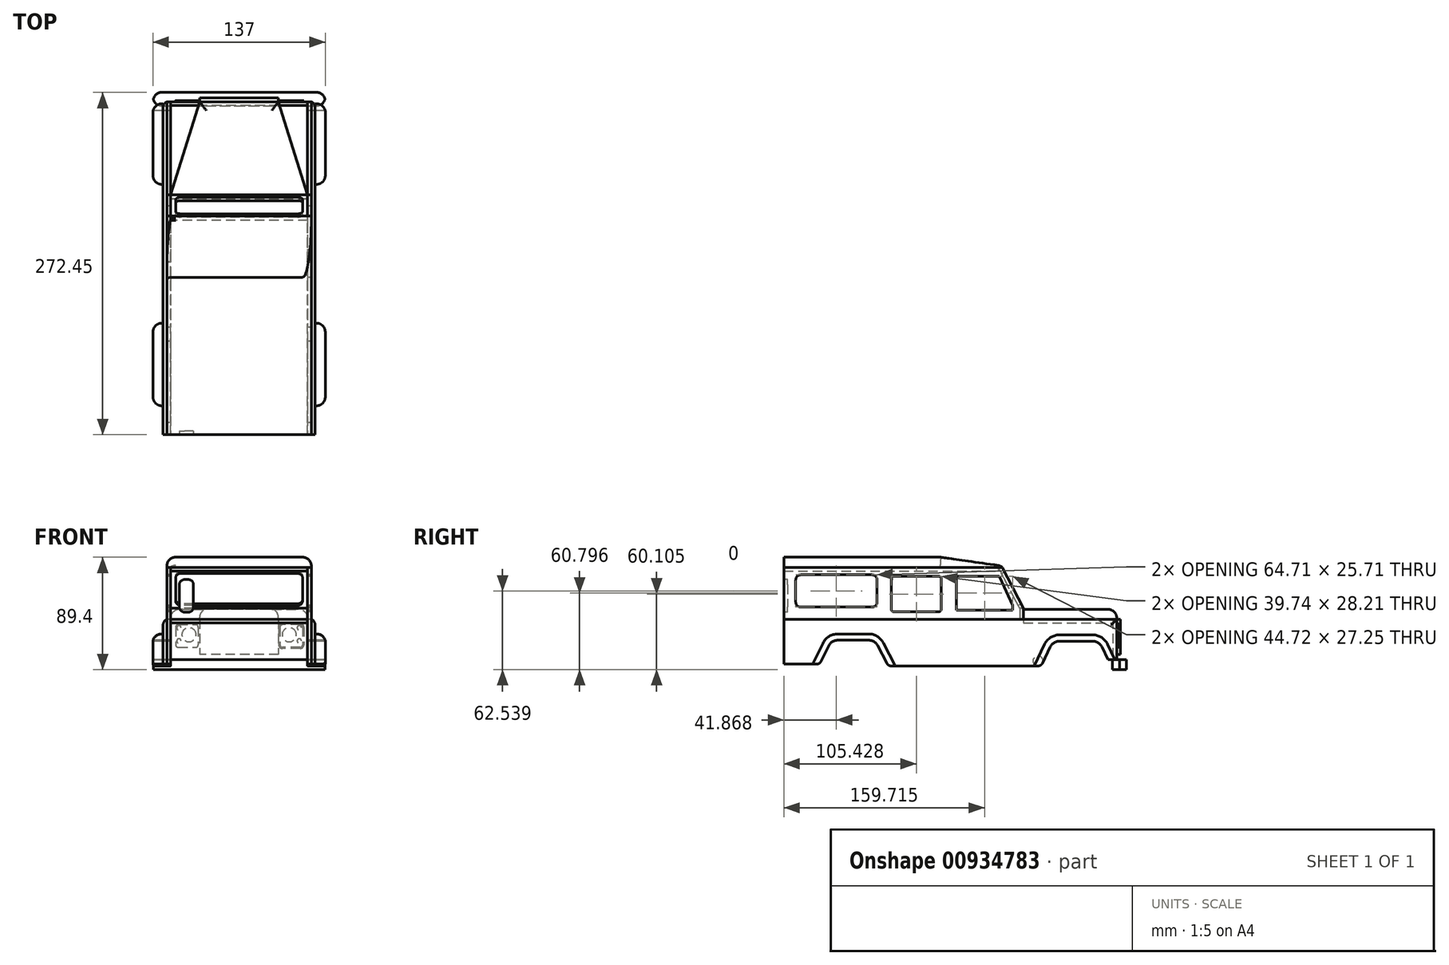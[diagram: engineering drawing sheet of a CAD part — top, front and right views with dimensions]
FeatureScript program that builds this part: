
annotation { "Feature Type Name" : "Feature", "Feature Type Description" : "" }
export const myFeature = defineFeature(function(context is Context, id is Id, definition is map)
    precondition{}
    {
        {
            var Q0;
            Q0=qCreatedBy(makeId("Right.planeOp"),FACE);
            var sketch = newSketch(context, id + "F0", { "sketchPlane" : qUnion([Q0])});
            skLineSegment(sketch, "E0", {"start": v(6.05, 16.68) * mm, "end": v(6.05, 93.72) * mm});
            skLineSegment(sketch, "E1", {"start": v(6.05, 93.72) * mm, "end": v(180.01, 93.72) * mm});
            skLineSegment(sketch, "E2", {"start": v(180.01, 93.72) * mm, "end": v(196.81, 61.17) * mm});
            skLineSegment(sketch, "E3", {"start": v(196.81, 61.17) * mm, "end": v(196.81, 52.3) * mm});
            skLineSegment(sketch, "E4", {"start": v(196.81, 52.3) * mm, "end": v(270.97, 52.3) * mm});
            skLineSegment(sketch, "E5", {"start": v(270.97, 52.3) * mm, "end": v(270.97, 20.32) * mm});
            skLineSegment(sketch, "E6", {"start": v(270.97, 20.32) * mm, "end": v(263.87, 20.32) * mm});
            skLineSegment(sketch, "E7", {"start": v(263.87, 20.32) * mm, "end": v(259.15, 30.3) * mm});
            skLineSegment(sketch, "E8", {"start": v(251.92, 34.88) * mm, "end": v(225.3, 34.88) * mm});
            skLineSegment(sketch, "E9", {"start": v(218.07, 30.32) * mm, "end": v(211.96, 17.47) * mm});
            skLineSegment(sketch, "E10", {"start": v(208.35, 15.2) * mm, "end": v(91.6, 15.2) * mm});
            skLineSegment(sketch, "E11", {"start": v(88.04, 17.34) * mm, "end": v(80.75, 31.36) * mm});
            skLineSegment(sketch, "E12", {"start": v(73.66, 35.66) * mm, "end": v(48.95, 35.66) * mm});
            skLineSegment(sketch, "E13", {"start": v(41.76, 31.17) * mm, "end": v(35.78, 18.92) * mm});
            skLineSegment(sketch, "E14", {"start": v(32.18, 16.68) * mm, "end": v(6.05, 16.68) * mm});
            skPoint(sketch, "E15.visualSharp", {"position": v(78.51, 35.66) * mm});
            skArc(sketch, "E15.filletArc", {"start": v(80.75, 31.36) * mm, "mid": v(77.8, 34.5) * mm, "end": v(73.66, 35.66) * mm});
            skPoint(sketch, "E16.visualSharp", {"position": v(43.95, 35.66) * mm});
            skArc(sketch, "E16.filletArc", {"start": v(48.95, 35.66) * mm, "mid": v(44.7, 34.45) * mm, "end": v(41.76, 31.17) * mm});
            skPoint(sketch, "E17.visualSharp", {"position": v(220.24, 34.88) * mm});
            skArc(sketch, "E17.filletArc", {"start": v(225.3, 34.88) * mm, "mid": v(221.02, 33.65) * mm, "end": v(218.07, 30.32) * mm});
            skPoint(sketch, "E18.visualSharp", {"position": v(256.99, 34.88) * mm});
            skArc(sketch, "E18.filletArc", {"start": v(259.15, 30.3) * mm, "mid": v(256.2, 33.64) * mm, "end": v(251.92, 34.88) * mm});
            skLineSegment(sketch, "E19", {"start": v(19.56, 87.71) * mm, "end": v(76.27, 87.71) * mm});
            skLineSegment(sketch, "E20", {"start": v(80.27, 83.71) * mm, "end": v(80.27, 66) * mm});
            skLineSegment(sketch, "E21", {"start": v(76.27, 62) * mm, "end": v(19.56, 62) * mm});
            skLineSegment(sketch, "E22", {"start": v(15.56, 66) * mm, "end": v(15.56, 83.71) * mm});
            skPoint(sketch, "E23.visualSharp", {"position": v(15.56, 87.71) * mm});
            skArc(sketch, "E23.filletArc", {"start": v(19.56, 87.71) * mm, "mid": v(16.73, 86.54) * mm, "end": v(15.56, 83.71) * mm});
            skPoint(sketch, "E24.visualSharp", {"position": v(80.27, 87.71) * mm});
            skArc(sketch, "E24.filletArc", {"start": v(80.27, 83.71) * mm, "mid": v(79.1, 86.54) * mm, "end": v(76.27, 87.71) * mm});
            skPoint(sketch, "E25.visualSharp", {"position": v(80.27, 62) * mm});
            skArc(sketch, "E25.filletArc", {"start": v(76.27, 62) * mm, "mid": v(79.1, 63.18) * mm, "end": v(80.27, 66) * mm});
            skPoint(sketch, "E26.visualSharp", {"position": v(15.56, 62) * mm});
            skArc(sketch, "E26.filletArc", {"start": v(15.56, 66) * mm, "mid": v(16.73, 63.18) * mm, "end": v(19.56, 62) * mm});
            skLineSegment(sketch, "E27", {"start": v(93.6, 86.53) * mm, "end": v(129.35, 86.53) * mm});
            skLineSegment(sketch, "E28", {"start": v(131.35, 84.53) * mm, "end": v(131.35, 60.32) * mm});
            skLineSegment(sketch, "E29", {"start": v(129.35, 58.32) * mm, "end": v(93.6, 58.32) * mm});
            skLineSegment(sketch, "E30", {"start": v(91.6, 60.32) * mm, "end": v(91.6, 84.53) * mm});
            skPoint(sketch, "E31.visualSharp", {"position": v(91.6, 86.53) * mm});
            skArc(sketch, "E31.filletArc", {"start": v(93.6, 86.53) * mm, "mid": v(92.2, 85.94) * mm, "end": v(91.6, 84.53) * mm});
            skPoint(sketch, "E32.visualSharp", {"position": v(131.35, 86.53) * mm});
            skArc(sketch, "E32.filletArc", {"start": v(131.35, 84.53) * mm, "mid": v(130.76, 85.94) * mm, "end": v(129.35, 86.53) * mm});
            skPoint(sketch, "E33.visualSharp", {"position": v(131.35, 58.32) * mm});
            skArc(sketch, "E33.filletArc", {"start": v(129.35, 58.32) * mm, "mid": v(130.76, 58.9) * mm, "end": v(131.35, 60.32) * mm});
            skPoint(sketch, "E34.visualSharp", {"position": v(91.6, 58.32) * mm});
            skArc(sketch, "E34.filletArc", {"start": v(91.6, 60.32) * mm, "mid": v(92.2, 58.9) * mm, "end": v(93.6, 58.32) * mm});
            skLineSegment(sketch, "E35", {"start": v(143.4, 86.74) * mm, "end": v(176.27, 86.74) * mm});
            skLineSegment(sketch, "E36", {"start": v(178.1, 85.57) * mm, "end": v(188.13, 63.5) * mm});
            skLineSegment(sketch, "E37", {"start": v(188.13, 63.5) * mm, "end": v(188.13, 59.49) * mm});
            skLineSegment(sketch, "E38", {"start": v(188.13, 59.49) * mm, "end": v(143.5, 59.49) * mm});
            skLineSegment(sketch, "E39", {"start": v(143.5, 59.49) * mm, "end": v(143.4, 86.74) * mm});
            skPoint(sketch, "E40.visualSharp", {"position": v(177.56, 86.74) * mm});
            skArc(sketch, "E40.filletArc", {"start": v(178.1, 85.57) * mm, "mid": v(177.35, 86.42) * mm, "end": v(176.27, 86.74) * mm});
            skPoint(sketch, "E41.visualSharp", {"position": v(210.87, 15.2) * mm});
            skArc(sketch, "E41.filletArc", {"start": v(208.35, 15.2) * mm, "mid": v(210.48, 15.8) * mm, "end": v(211.96, 17.47) * mm});
            skPoint(sketch, "E42.visualSharp", {"position": v(89.16, 15.2) * mm});
            skArc(sketch, "E42.filletArc", {"start": v(88.04, 17.34) * mm, "mid": v(89.52, 15.77) * mm, "end": v(91.6, 15.2) * mm});
            skPoint(sketch, "E43.visualSharp", {"position": v(34.68, 16.68) * mm});
            skArc(sketch, "E43.filletArc", {"start": v(32.18, 16.68) * mm, "mid": v(34.3, 17.29) * mm, "end": v(35.78, 18.92) * mm});
            skSolve(sketch);
        }
        {
            var Q0;
            Q0=makeQuery(id+"F0.imprint","IMPRINT",FACE,{"disambiguationData":[TD([[makeQuery(id+"F0.imprint","IMPRINT",EDGE,{"derivedFrom":sQuery(id+"F0.wireOp",EDGE,"E0")}),-1.0]])]});
            extrude(context, id + "F1", {"entities" : qUnion([Q0]), "depth" : 3 * mm, "offsetDistance" : 25 * mm});
        }
        {
            var Q0;
            Q0=makeQuery(id+"F1.opExtrude","SWEPT_BODY",BODY,{"disambiguationData":[OSD([sQuery(id+"F0.wireOp",EDGE,"E0"),sQuery(id+"F0.wireOp",EDGE,"E1"),sQuery(id+"F0.wireOp",EDGE,"E2"),sQuery(id+"F0.wireOp",EDGE,"E3"),sQuery(id+"F0.wireOp",EDGE,"E4"),sQuery(id+"F0.wireOp",EDGE,"E5"),sQuery(id+"F0.wireOp",EDGE,"E6"),sQuery(id+"F0.wireOp",EDGE,"E7"),sQuery(id+"F0.wireOp",EDGE,"E8"),sQuery(id+"F0.wireOp",EDGE,"E9"),sQuery(id+"F0.wireOp",EDGE,"E10"),sQuery(id+"F0.wireOp",EDGE,"E11"),sQuery(id+"F0.wireOp",EDGE,"E12"),sQuery(id+"F0.wireOp",EDGE,"E13"),sQuery(id+"F0.wireOp",EDGE,"E14"),sQuery(id+"F0.wireOp",EDGE,"E15.filletArc"),sQuery(id+"F0.wireOp",EDGE,"E16.filletArc"),sQuery(id+"F0.wireOp",EDGE,"E17.filletArc"),sQuery(id+"F0.wireOp",EDGE,"E18.filletArc"),sQuery(id+"F0.wireOp",EDGE,"E19"),sQuery(id+"F0.wireOp",EDGE,"E20"),sQuery(id+"F0.wireOp",EDGE,"E21"),sQuery(id+"F0.wireOp",EDGE,"E22"),sQuery(id+"F0.wireOp",EDGE,"E23.filletArc"),sQuery(id+"F0.wireOp",EDGE,"E24.filletArc"),sQuery(id+"F0.wireOp",EDGE,"E25.filletArc"),sQuery(id+"F0.wireOp",EDGE,"E26.filletArc"),sQuery(id+"F0.wireOp",EDGE,"E27"),sQuery(id+"F0.wireOp",EDGE,"E28"),sQuery(id+"F0.wireOp",EDGE,"E29"),sQuery(id+"F0.wireOp",EDGE,"E30"),sQuery(id+"F0.wireOp",EDGE,"E31.filletArc"),sQuery(id+"F0.wireOp",EDGE,"E32.filletArc"),sQuery(id+"F0.wireOp",EDGE,"E33.filletArc"),sQuery(id+"F0.wireOp",EDGE,"E34.filletArc"),sQuery(id+"F0.wireOp",EDGE,"E35"),sQuery(id+"F0.wireOp",EDGE,"E36"),sQuery(id+"F0.wireOp",EDGE,"E37"),sQuery(id+"F0.wireOp",EDGE,"E38"),sQuery(id+"F0.wireOp",EDGE,"E39"),sQuery(id+"F0.wireOp",EDGE,"E40.filletArc")])]});
            transform(context, id + "F2", {"entities" : qUnion([Q0]), "transformType" : TransformType.TRANSLATION_3D, "dx" : 112 * mm, "dy" : 0 * mm, "dz" : 0 * mm, "makeCopy" : true});
        }
        {
            var Q0;
            Q0=makeQuery(id+"F1.opExtrude","CAP_FACE",FACE,{"disambiguationData":[OSD([sQuery(id+"F0.wireOp",EDGE,"E0"),sQuery(id+"F0.wireOp",EDGE,"E1"),sQuery(id+"F0.wireOp",EDGE,"E2"),sQuery(id+"F0.wireOp",EDGE,"E3"),sQuery(id+"F0.wireOp",EDGE,"E4"),sQuery(id+"F0.wireOp",EDGE,"E5"),sQuery(id+"F0.wireOp",EDGE,"E6"),sQuery(id+"F0.wireOp",EDGE,"E7"),sQuery(id+"F0.wireOp",EDGE,"E8"),sQuery(id+"F0.wireOp",EDGE,"E9"),sQuery(id+"F0.wireOp",EDGE,"E10"),sQuery(id+"F0.wireOp",EDGE,"E11"),sQuery(id+"F0.wireOp",EDGE,"E12"),sQuery(id+"F0.wireOp",EDGE,"E13"),sQuery(id+"F0.wireOp",EDGE,"E14"),sQuery(id+"F0.wireOp",EDGE,"E15.filletArc"),sQuery(id+"F0.wireOp",EDGE,"E16.filletArc"),sQuery(id+"F0.wireOp",EDGE,"E17.filletArc"),sQuery(id+"F0.wireOp",EDGE,"E18.filletArc"),sQuery(id+"F0.wireOp",EDGE,"E19"),sQuery(id+"F0.wireOp",EDGE,"E20"),sQuery(id+"F0.wireOp",EDGE,"E21"),sQuery(id+"F0.wireOp",EDGE,"E22"),sQuery(id+"F0.wireOp",EDGE,"E23.filletArc"),sQuery(id+"F0.wireOp",EDGE,"E24.filletArc"),sQuery(id+"F0.wireOp",EDGE,"E25.filletArc"),sQuery(id+"F0.wireOp",EDGE,"E26.filletArc"),sQuery(id+"F0.wireOp",EDGE,"E27"),sQuery(id+"F0.wireOp",EDGE,"E28"),sQuery(id+"F0.wireOp",EDGE,"E29"),sQuery(id+"F0.wireOp",EDGE,"E30"),sQuery(id+"F0.wireOp",EDGE,"E31.filletArc"),sQuery(id+"F0.wireOp",EDGE,"E32.filletArc"),sQuery(id+"F0.wireOp",EDGE,"E33.filletArc"),sQuery(id+"F0.wireOp",EDGE,"E34.filletArc"),sQuery(id+"F0.wireOp",EDGE,"E35"),sQuery(id+"F0.wireOp",EDGE,"E36"),sQuery(id+"F0.wireOp",EDGE,"E37"),sQuery(id+"F0.wireOp",EDGE,"E38"),sQuery(id+"F0.wireOp",EDGE,"E39"),sQuery(id+"F0.wireOp",EDGE,"E40.filletArc")])],"isStart":false});
            var sketch = newSketch(context, id + "F3", { "sketchPlane" : qUnion([Q0])});
            skLineSegment(sketch, "E44.bottom", {"start": v(270.97, 52.3) * mm, "end": v(267.97, 52.3) * mm});
            skLineSegment(sketch, "E44.top", {"start": v(270.97, 20.32) * mm, "end": v(267.97, 20.32) * mm});
            skLineSegment(sketch, "E44.left", {"start": v(270.97, 52.3) * mm, "end": v(270.97, 20.32) * mm});
            skLineSegment(sketch, "E44.right", {"start": v(267.97, 52.3) * mm, "end": v(267.97, 20.32) * mm});
            skSolve(sketch);
        }
        {
            var Q0;
            Q0=makeQuery(id+"F3.imprint","IMPRINT",FACE,{"disambiguationData":[TD([[makeQuery(id+"F3.imprint","IMPRINT",EDGE,{"derivedFrom":sQuery(id+"F3.wireOp",EDGE,"E44.bottom")}),-1.0]])]});
            extrude(context, id + "F4", {"entities" : qUnion([Q0]), "endBound" : BoundingType.UP_TO_NEXT, "depth" : 25 * mm, "offsetDistance" : 25 * mm});
        }
        {
            var Q0;
            Q0=makeQuery(id+"F1.opExtrude","CAP_FACE",FACE,{"disambiguationData":[OSD([sQuery(id+"F0.wireOp",EDGE,"E0"),sQuery(id+"F0.wireOp",EDGE,"E1"),sQuery(id+"F0.wireOp",EDGE,"E2"),sQuery(id+"F0.wireOp",EDGE,"E3"),sQuery(id+"F0.wireOp",EDGE,"E4"),sQuery(id+"F0.wireOp",EDGE,"E5"),sQuery(id+"F0.wireOp",EDGE,"E6"),sQuery(id+"F0.wireOp",EDGE,"E7"),sQuery(id+"F0.wireOp",EDGE,"E8"),sQuery(id+"F0.wireOp",EDGE,"E9"),sQuery(id+"F0.wireOp",EDGE,"E10"),sQuery(id+"F0.wireOp",EDGE,"E11"),sQuery(id+"F0.wireOp",EDGE,"E12"),sQuery(id+"F0.wireOp",EDGE,"E13"),sQuery(id+"F0.wireOp",EDGE,"E14"),sQuery(id+"F0.wireOp",EDGE,"E15.filletArc"),sQuery(id+"F0.wireOp",EDGE,"E16.filletArc"),sQuery(id+"F0.wireOp",EDGE,"E17.filletArc"),sQuery(id+"F0.wireOp",EDGE,"E18.filletArc"),sQuery(id+"F0.wireOp",EDGE,"E19"),sQuery(id+"F0.wireOp",EDGE,"E20"),sQuery(id+"F0.wireOp",EDGE,"E21"),sQuery(id+"F0.wireOp",EDGE,"E22"),sQuery(id+"F0.wireOp",EDGE,"E23.filletArc"),sQuery(id+"F0.wireOp",EDGE,"E24.filletArc"),sQuery(id+"F0.wireOp",EDGE,"E25.filletArc"),sQuery(id+"F0.wireOp",EDGE,"E26.filletArc"),sQuery(id+"F0.wireOp",EDGE,"E27"),sQuery(id+"F0.wireOp",EDGE,"E28"),sQuery(id+"F0.wireOp",EDGE,"E29"),sQuery(id+"F0.wireOp",EDGE,"E30"),sQuery(id+"F0.wireOp",EDGE,"E31.filletArc"),sQuery(id+"F0.wireOp",EDGE,"E32.filletArc"),sQuery(id+"F0.wireOp",EDGE,"E33.filletArc"),sQuery(id+"F0.wireOp",EDGE,"E34.filletArc"),sQuery(id+"F0.wireOp",EDGE,"E35"),sQuery(id+"F0.wireOp",EDGE,"E36"),sQuery(id+"F0.wireOp",EDGE,"E37"),sQuery(id+"F0.wireOp",EDGE,"E38"),sQuery(id+"F0.wireOp",EDGE,"E39"),sQuery(id+"F0.wireOp",EDGE,"E40.filletArc")])],"isStart":false});
            var sketch = newSketch(context, id + "F5", { "sketchPlane" : qUnion([Q0])});
            skLineSegment(sketch, "E45.bottom", {"start": v(196.81, 52.3) * mm, "end": v(267.97, 52.3) * mm});
            skLineSegment(sketch, "E45.top", {"start": v(196.81, 49.3) * mm, "end": v(267.97, 49.3) * mm});
            skLineSegment(sketch, "E45.left", {"start": v(196.81, 52.3) * mm, "end": v(196.81, 49.3) * mm});
            skLineSegment(sketch, "E45.right", {"start": v(267.97, 52.3) * mm, "end": v(267.97, 49.3) * mm});
            skSolve(sketch);
        }
        {
            var Q0;
            Q0 = qSketchRegion(id + "F5", true);
            extrude(context, id + "F6", {"entities" : qUnion([Q0]), "endBound" : BoundingType.UP_TO_NEXT, "depth" : 25 * mm, "offsetDistance" : 25 * mm});
        }
        {
            var Q0;
            Q0=makeQuery(id+"F1.opExtrude","CAP_FACE",FACE,{"disambiguationData":[OSD([sQuery(id+"F0.wireOp",EDGE,"E0"),sQuery(id+"F0.wireOp",EDGE,"E1"),sQuery(id+"F0.wireOp",EDGE,"E2"),sQuery(id+"F0.wireOp",EDGE,"E3"),sQuery(id+"F0.wireOp",EDGE,"E4"),sQuery(id+"F0.wireOp",EDGE,"E5"),sQuery(id+"F0.wireOp",EDGE,"E6"),sQuery(id+"F0.wireOp",EDGE,"E7"),sQuery(id+"F0.wireOp",EDGE,"E8"),sQuery(id+"F0.wireOp",EDGE,"E9"),sQuery(id+"F0.wireOp",EDGE,"E10"),sQuery(id+"F0.wireOp",EDGE,"E11"),sQuery(id+"F0.wireOp",EDGE,"E12"),sQuery(id+"F0.wireOp",EDGE,"E13"),sQuery(id+"F0.wireOp",EDGE,"E14"),sQuery(id+"F0.wireOp",EDGE,"E15.filletArc"),sQuery(id+"F0.wireOp",EDGE,"E16.filletArc"),sQuery(id+"F0.wireOp",EDGE,"E17.filletArc"),sQuery(id+"F0.wireOp",EDGE,"E18.filletArc"),sQuery(id+"F0.wireOp",EDGE,"E19"),sQuery(id+"F0.wireOp",EDGE,"E20"),sQuery(id+"F0.wireOp",EDGE,"E21"),sQuery(id+"F0.wireOp",EDGE,"E22"),sQuery(id+"F0.wireOp",EDGE,"E23.filletArc"),sQuery(id+"F0.wireOp",EDGE,"E24.filletArc"),sQuery(id+"F0.wireOp",EDGE,"E25.filletArc"),sQuery(id+"F0.wireOp",EDGE,"E26.filletArc"),sQuery(id+"F0.wireOp",EDGE,"E27"),sQuery(id+"F0.wireOp",EDGE,"E28"),sQuery(id+"F0.wireOp",EDGE,"E29"),sQuery(id+"F0.wireOp",EDGE,"E30"),sQuery(id+"F0.wireOp",EDGE,"E31.filletArc"),sQuery(id+"F0.wireOp",EDGE,"E32.filletArc"),sQuery(id+"F0.wireOp",EDGE,"E33.filletArc"),sQuery(id+"F0.wireOp",EDGE,"E34.filletArc"),sQuery(id+"F0.wireOp",EDGE,"E35"),sQuery(id+"F0.wireOp",EDGE,"E36"),sQuery(id+"F0.wireOp",EDGE,"E37"),sQuery(id+"F0.wireOp",EDGE,"E38"),sQuery(id+"F0.wireOp",EDGE,"E39"),sQuery(id+"F0.wireOp",EDGE,"E40.filletArc")])],"isStart":false});
            var sketch = newSketch(context, id + "F7", { "sketchPlane" : qUnion([Q0])});
            skLineSegment(sketch, "E46.bottom", {"start": v(196.81, 61.17) * mm, "end": v(193.81, 61.17) * mm});
            skLineSegment(sketch, "E46.top", {"start": v(196.81, 52.3) * mm, "end": v(193.81, 52.3) * mm});
            skLineSegment(sketch, "E46.left", {"start": v(196.81, 61.17) * mm, "end": v(196.81, 52.3) * mm});
            skLineSegment(sketch, "E46.right", {"start": v(193.81, 61.17) * mm, "end": v(193.81, 52.3) * mm});
            skSolve(sketch);
        }
        {
            var Q0;
            Q0=makeQuery(id+"F7.imprint","IMPRINT",FACE,{"disambiguationData":[TD([[makeQuery(id+"F7.imprint","IMPRINT",EDGE,{"derivedFrom":sQuery(id+"F7.wireOp",EDGE,"E46.bottom")}),1.0]])]});
            extrude(context, id + "F8", {"entities" : qUnion([Q0]), "endBound" : BoundingType.UP_TO_NEXT, "depth" : 25 * mm, "offsetDistance" : 25 * mm});
        }
        {
            var Q0;
            Q0=makeQuery(id+"F1.opExtrude","CAP_FACE",FACE,{"disambiguationData":[OSD([sQuery(id+"F0.wireOp",EDGE,"E0"),sQuery(id+"F0.wireOp",EDGE,"E1"),sQuery(id+"F0.wireOp",EDGE,"E2"),sQuery(id+"F0.wireOp",EDGE,"E3"),sQuery(id+"F0.wireOp",EDGE,"E4"),sQuery(id+"F0.wireOp",EDGE,"E5"),sQuery(id+"F0.wireOp",EDGE,"E6"),sQuery(id+"F0.wireOp",EDGE,"E7"),sQuery(id+"F0.wireOp",EDGE,"E8"),sQuery(id+"F0.wireOp",EDGE,"E9"),sQuery(id+"F0.wireOp",EDGE,"E10"),sQuery(id+"F0.wireOp",EDGE,"E11"),sQuery(id+"F0.wireOp",EDGE,"E12"),sQuery(id+"F0.wireOp",EDGE,"E13"),sQuery(id+"F0.wireOp",EDGE,"E14"),sQuery(id+"F0.wireOp",EDGE,"E15.filletArc"),sQuery(id+"F0.wireOp",EDGE,"E16.filletArc"),sQuery(id+"F0.wireOp",EDGE,"E17.filletArc"),sQuery(id+"F0.wireOp",EDGE,"E18.filletArc"),sQuery(id+"F0.wireOp",EDGE,"E19"),sQuery(id+"F0.wireOp",EDGE,"E20"),sQuery(id+"F0.wireOp",EDGE,"E21"),sQuery(id+"F0.wireOp",EDGE,"E22"),sQuery(id+"F0.wireOp",EDGE,"E23.filletArc"),sQuery(id+"F0.wireOp",EDGE,"E24.filletArc"),sQuery(id+"F0.wireOp",EDGE,"E25.filletArc"),sQuery(id+"F0.wireOp",EDGE,"E26.filletArc"),sQuery(id+"F0.wireOp",EDGE,"E27"),sQuery(id+"F0.wireOp",EDGE,"E28"),sQuery(id+"F0.wireOp",EDGE,"E29"),sQuery(id+"F0.wireOp",EDGE,"E30"),sQuery(id+"F0.wireOp",EDGE,"E31.filletArc"),sQuery(id+"F0.wireOp",EDGE,"E32.filletArc"),sQuery(id+"F0.wireOp",EDGE,"E33.filletArc"),sQuery(id+"F0.wireOp",EDGE,"E34.filletArc"),sQuery(id+"F0.wireOp",EDGE,"E35"),sQuery(id+"F0.wireOp",EDGE,"E36"),sQuery(id+"F0.wireOp",EDGE,"E37"),sQuery(id+"F0.wireOp",EDGE,"E38"),sQuery(id+"F0.wireOp",EDGE,"E39"),sQuery(id+"F0.wireOp",EDGE,"E40.filletArc")])],"isStart":false});
            var sketch = newSketch(context, id + "F9", { "sketchPlane" : qUnion([Q0])});
            skLineSegment(sketch, "E47", {"start": v(180.01, 93.72) * mm, "end": v(176.63, 93.72) * mm});
            skLineSegment(sketch, "E48", {"start": v(176.63, 93.72) * mm, "end": v(193.44, 61.17) * mm});
            skLineSegment(sketch, "E49", {"start": v(193.44, 61.17) * mm, "end": v(196.81, 61.17) * mm});
            skLineSegment(sketch, "E50", {"start": v(196.81, 61.17) * mm, "end": v(180.01, 93.72) * mm});
            skSolve(sketch);
        }
        {
            var Q0;
            Q0=makeQuery(id+"F9.imprint","IMPRINT",FACE,{"disambiguationData":[TD([[makeQuery(id+"F9.imprint","IMPRINT",EDGE,{"derivedFrom":sQuery(id+"F9.wireOp",EDGE,"E47")}),-1.0]])]});
            extrude(context, id + "F10", {"entities" : qUnion([Q0]), "endBound" : BoundingType.UP_TO_NEXT, "depth" : 25 * mm, "offsetDistance" : 25 * mm});
        }
        {
            var Q0;
            Q0=makeQuery(id+"F10.opExtrude","SWEPT_FACE",FACE,{"disambiguationData":[OSD([sQuery(id+"F9.wireOp",EDGE,"E50")])]});
            var sketch = newSketch(context, id + "F11", { "sketchPlane" : qUnion([Q0])});
            skLineSegment(sketch, "E51.bottom", {"start": v(-104, -3.3) * mm, "end": v(-11, -3.3) * mm});
            skLineSegment(sketch, "E51.top", {"start": v(-104, -31.93) * mm, "end": v(-11, -31.93) * mm});
            skLineSegment(sketch, "E51.left", {"start": v(-108, -7.3) * mm, "end": v(-108, -27.93) * mm});
            skLineSegment(sketch, "E51.right", {"start": v(-7, -7.3) * mm, "end": v(-7, -27.93) * mm});
            skPoint(sketch, "E52.visualSharp", {"position": v(-108, -3.3) * mm});
            skArc(sketch, "E52.filletArc", {"start": v(-104, -3.3) * mm, "mid": v(-106.83, -4.48) * mm, "end": v(-108, -7.3) * mm});
            skPoint(sketch, "E53.visualSharp", {"position": v(-7, -3.3) * mm});
            skArc(sketch, "E53.filletArc", {"start": v(-7, -7.3) * mm, "mid": v(-8.17, -4.48) * mm, "end": v(-11, -3.3) * mm});
            skPoint(sketch, "E54.visualSharp", {"position": v(-7, -31.93) * mm});
            skArc(sketch, "E54.filletArc", {"start": v(-11, -31.93) * mm, "mid": v(-8.17, -30.76) * mm, "end": v(-7, -27.93) * mm});
            skPoint(sketch, "E55.visualSharp", {"position": v(-108, -31.93) * mm});
            skArc(sketch, "E55.filletArc", {"start": v(-108, -27.93) * mm, "mid": v(-106.83, -30.76) * mm, "end": v(-104, -31.93) * mm});
            skSolve(sketch);
        }
        {
            var Q0;
            Q0=makeQuery(id+"F11.imprint","IMPRINT",FACE,{"disambiguationData":[TD([[makeQuery(id+"F11.imprint","IMPRINT",EDGE,{"derivedFrom":sQuery(id+"F11.wireOp",EDGE,"E51.bottom")}),-1.0]])]});
            extrude(context, id + "F12", {"entities" : qUnion([Q0]), "operationType" : NewBodyOperationType.REMOVE, "oppositeDirection" : true, "depth" : 20.7 * mm, "offsetDistance" : 25 * mm});
        }
        {
            var Q0;
            Q0=makeQuery(id+"F1.opExtrude","CAP_FACE",FACE,{"disambiguationData":[OSD([sQuery(id+"F0.wireOp",EDGE,"E0"),sQuery(id+"F0.wireOp",EDGE,"E1"),sQuery(id+"F0.wireOp",EDGE,"E2"),sQuery(id+"F0.wireOp",EDGE,"E3"),sQuery(id+"F0.wireOp",EDGE,"E4"),sQuery(id+"F0.wireOp",EDGE,"E5"),sQuery(id+"F0.wireOp",EDGE,"E6"),sQuery(id+"F0.wireOp",EDGE,"E7"),sQuery(id+"F0.wireOp",EDGE,"E8"),sQuery(id+"F0.wireOp",EDGE,"E9"),sQuery(id+"F0.wireOp",EDGE,"E10"),sQuery(id+"F0.wireOp",EDGE,"E11"),sQuery(id+"F0.wireOp",EDGE,"E12"),sQuery(id+"F0.wireOp",EDGE,"E13"),sQuery(id+"F0.wireOp",EDGE,"E14"),sQuery(id+"F0.wireOp",EDGE,"E15.filletArc"),sQuery(id+"F0.wireOp",EDGE,"E16.filletArc"),sQuery(id+"F0.wireOp",EDGE,"E17.filletArc"),sQuery(id+"F0.wireOp",EDGE,"E18.filletArc"),sQuery(id+"F0.wireOp",EDGE,"E19"),sQuery(id+"F0.wireOp",EDGE,"E20"),sQuery(id+"F0.wireOp",EDGE,"E21"),sQuery(id+"F0.wireOp",EDGE,"E22"),sQuery(id+"F0.wireOp",EDGE,"E23.filletArc"),sQuery(id+"F0.wireOp",EDGE,"E24.filletArc"),sQuery(id+"F0.wireOp",EDGE,"E25.filletArc"),sQuery(id+"F0.wireOp",EDGE,"E26.filletArc"),sQuery(id+"F0.wireOp",EDGE,"E27"),sQuery(id+"F0.wireOp",EDGE,"E28"),sQuery(id+"F0.wireOp",EDGE,"E29"),sQuery(id+"F0.wireOp",EDGE,"E30"),sQuery(id+"F0.wireOp",EDGE,"E31.filletArc"),sQuery(id+"F0.wireOp",EDGE,"E32.filletArc"),sQuery(id+"F0.wireOp",EDGE,"E33.filletArc"),sQuery(id+"F0.wireOp",EDGE,"E34.filletArc"),sQuery(id+"F0.wireOp",EDGE,"E35"),sQuery(id+"F0.wireOp",EDGE,"E36"),sQuery(id+"F0.wireOp",EDGE,"E37"),sQuery(id+"F0.wireOp",EDGE,"E38"),sQuery(id+"F0.wireOp",EDGE,"E39"),sQuery(id+"F0.wireOp",EDGE,"E40.filletArc")])],"isStart":false});
            var sketch = newSketch(context, id + "F13", { "sketchPlane" : qUnion([Q0])});
            skLineSegment(sketch, "E56.bottom", {"start": v(6.05, 93.72) * mm, "end": v(176.63, 93.72) * mm});
            skLineSegment(sketch, "E56.top", {"start": v(6.05, 90.72) * mm, "end": v(176.63, 90.72) * mm});
            skLineSegment(sketch, "E56.left", {"start": v(6.05, 93.72) * mm, "end": v(6.05, 90.72) * mm});
            skLineSegment(sketch, "E56.right", {"start": v(176.63, 93.72) * mm, "end": v(176.63, 90.72) * mm});
            skSolve(sketch);
        }
        {
            var Q0;
            Q0=makeQuery(id+"F13.imprint","IMPRINT",FACE,{"disambiguationData":[TD([[makeQuery(id+"F13.imprint","IMPRINT",EDGE,{"derivedFrom":sQuery(id+"F13.wireOp",EDGE,"E56.bottom")}),-1.0]])]});
            extrude(context, id + "F14", {"entities" : qUnion([Q0]), "endBound" : BoundingType.UP_TO_NEXT, "depth" : 25 * mm, "offsetDistance" : 25 * mm});
        }
        {
            var Q0;
            Q0=makeQuery(id+"F1.opExtrude","CAP_FACE",FACE,{"disambiguationData":[OSD([sQuery(id+"F0.wireOp",EDGE,"E0"),sQuery(id+"F0.wireOp",EDGE,"E1"),sQuery(id+"F0.wireOp",EDGE,"E2"),sQuery(id+"F0.wireOp",EDGE,"E3"),sQuery(id+"F0.wireOp",EDGE,"E4"),sQuery(id+"F0.wireOp",EDGE,"E5"),sQuery(id+"F0.wireOp",EDGE,"E6"),sQuery(id+"F0.wireOp",EDGE,"E7"),sQuery(id+"F0.wireOp",EDGE,"E8"),sQuery(id+"F0.wireOp",EDGE,"E9"),sQuery(id+"F0.wireOp",EDGE,"E10"),sQuery(id+"F0.wireOp",EDGE,"E11"),sQuery(id+"F0.wireOp",EDGE,"E12"),sQuery(id+"F0.wireOp",EDGE,"E13"),sQuery(id+"F0.wireOp",EDGE,"E14"),sQuery(id+"F0.wireOp",EDGE,"E15.filletArc"),sQuery(id+"F0.wireOp",EDGE,"E16.filletArc"),sQuery(id+"F0.wireOp",EDGE,"E17.filletArc"),sQuery(id+"F0.wireOp",EDGE,"E18.filletArc"),sQuery(id+"F0.wireOp",EDGE,"E19"),sQuery(id+"F0.wireOp",EDGE,"E20"),sQuery(id+"F0.wireOp",EDGE,"E21"),sQuery(id+"F0.wireOp",EDGE,"E22"),sQuery(id+"F0.wireOp",EDGE,"E23.filletArc"),sQuery(id+"F0.wireOp",EDGE,"E24.filletArc"),sQuery(id+"F0.wireOp",EDGE,"E25.filletArc"),sQuery(id+"F0.wireOp",EDGE,"E26.filletArc"),sQuery(id+"F0.wireOp",EDGE,"E27"),sQuery(id+"F0.wireOp",EDGE,"E28"),sQuery(id+"F0.wireOp",EDGE,"E29"),sQuery(id+"F0.wireOp",EDGE,"E30"),sQuery(id+"F0.wireOp",EDGE,"E31.filletArc"),sQuery(id+"F0.wireOp",EDGE,"E32.filletArc"),sQuery(id+"F0.wireOp",EDGE,"E33.filletArc"),sQuery(id+"F0.wireOp",EDGE,"E34.filletArc"),sQuery(id+"F0.wireOp",EDGE,"E35"),sQuery(id+"F0.wireOp",EDGE,"E36"),sQuery(id+"F0.wireOp",EDGE,"E37"),sQuery(id+"F0.wireOp",EDGE,"E38"),sQuery(id+"F0.wireOp",EDGE,"E39"),sQuery(id+"F0.wireOp",EDGE,"E40.filletArc")])],"isStart":false});
            var sketch = newSketch(context, id + "F15", { "sketchPlane" : qUnion([Q0])});
            skLineSegment(sketch, "E57.bottom", {"start": v(6.05, 16.68) * mm, "end": v(9.05, 16.68) * mm});
            skLineSegment(sketch, "E57.top", {"start": v(6.05, 90.72) * mm, "end": v(9.05, 90.72) * mm});
            skLineSegment(sketch, "E57.left", {"start": v(6.05, 16.68) * mm, "end": v(6.05, 90.72) * mm});
            skLineSegment(sketch, "E57.right", {"start": v(9.05, 16.68) * mm, "end": v(9.05, 90.72) * mm});
            skSolve(sketch);
        }
        {
            var Q0;
            Q0=makeQuery(id+"F15.imprint","IMPRINT",FACE,{"disambiguationData":[TD([[makeQuery(id+"F15.imprint","IMPRINT",EDGE,{"derivedFrom":sQuery(id+"F15.wireOp",EDGE,"E57.bottom")}),-1.0]])]});
            extrude(context, id + "F16", {"entities" : qUnion([Q0]), "endBound" : BoundingType.UP_TO_NEXT, "depth" : 25 * mm, "offsetDistance" : 25 * mm});
        }
        {
            var Q0;
            Q0=makeQuery(id+"F2.opPattern","COPY",FACE,{"derivedFrom":makeQuery(id+"F1.opExtrude","CAP_FACE",FACE,{"disambiguationData":[OSD([sQuery(id+"F0.wireOp",EDGE,"E0"),sQuery(id+"F0.wireOp",EDGE,"E1"),sQuery(id+"F0.wireOp",EDGE,"E2"),sQuery(id+"F0.wireOp",EDGE,"E3"),sQuery(id+"F0.wireOp",EDGE,"E4"),sQuery(id+"F0.wireOp",EDGE,"E5"),sQuery(id+"F0.wireOp",EDGE,"E6"),sQuery(id+"F0.wireOp",EDGE,"E7"),sQuery(id+"F0.wireOp",EDGE,"E8"),sQuery(id+"F0.wireOp",EDGE,"E9"),sQuery(id+"F0.wireOp",EDGE,"E10"),sQuery(id+"F0.wireOp",EDGE,"E11"),sQuery(id+"F0.wireOp",EDGE,"E12"),sQuery(id+"F0.wireOp",EDGE,"E13"),sQuery(id+"F0.wireOp",EDGE,"E14"),sQuery(id+"F0.wireOp",EDGE,"E15.filletArc"),sQuery(id+"F0.wireOp",EDGE,"E16.filletArc"),sQuery(id+"F0.wireOp",EDGE,"E17.filletArc"),sQuery(id+"F0.wireOp",EDGE,"E18.filletArc"),sQuery(id+"F0.wireOp",EDGE,"E19"),sQuery(id+"F0.wireOp",EDGE,"E20"),sQuery(id+"F0.wireOp",EDGE,"E21"),sQuery(id+"F0.wireOp",EDGE,"E22"),sQuery(id+"F0.wireOp",EDGE,"E23.filletArc"),sQuery(id+"F0.wireOp",EDGE,"E24.filletArc"),sQuery(id+"F0.wireOp",EDGE,"E25.filletArc"),sQuery(id+"F0.wireOp",EDGE,"E26.filletArc"),sQuery(id+"F0.wireOp",EDGE,"E27"),sQuery(id+"F0.wireOp",EDGE,"E28"),sQuery(id+"F0.wireOp",EDGE,"E29"),sQuery(id+"F0.wireOp",EDGE,"E30"),sQuery(id+"F0.wireOp",EDGE,"E31.filletArc"),sQuery(id+"F0.wireOp",EDGE,"E32.filletArc"),sQuery(id+"F0.wireOp",EDGE,"E33.filletArc"),sQuery(id+"F0.wireOp",EDGE,"E34.filletArc"),sQuery(id+"F0.wireOp",EDGE,"E35"),sQuery(id+"F0.wireOp",EDGE,"E36"),sQuery(id+"F0.wireOp",EDGE,"E37"),sQuery(id+"F0.wireOp",EDGE,"E38"),sQuery(id+"F0.wireOp",EDGE,"E39"),sQuery(id+"F0.wireOp",EDGE,"E40.filletArc")])],"isStart":false}),"instanceName":"1"});
            var sketch = newSketch(context, id + "F17", { "sketchPlane" : qUnion([Q0])});
            skLineSegment(sketch, "E58", {"start": v(196.81, 52.3) * mm, "end": v(6.05, 52.3) * mm});
            skSolve(sketch);
        }
        {
            var Q0;
            {var subQ0=sQuery(id+"F17.wireOp",EDGE,"E58");Q0=makeQuery(id+"F17.imprint","IMPRINT",FACE,{"disambiguationData":[TD([[makeQuery(id+"F17.imprint","IMPRINT",EDGE,{"derivedFrom":subQ0}),1.0]])]});}
            extrude(context, id + "F18", {"entities" : qUnion([Q0]), "depth" : 3 * mm, "offsetDistance" : 25 * mm});
        }
        {
            var Q0;
            Q0=makeQuery(id+"F18.opExtrude","SWEPT_BODY",BODY,{"disambiguationData":[OSD([sQuery(id+"F0.wireOp",EDGE,"E0"),sQuery(id+"F0.wireOp",EDGE,"E4"),sQuery(id+"F0.wireOp",EDGE,"E5"),sQuery(id+"F0.wireOp",EDGE,"E6"),sQuery(id+"F0.wireOp",EDGE,"E7"),sQuery(id+"F0.wireOp",EDGE,"E8"),sQuery(id+"F0.wireOp",EDGE,"E9"),sQuery(id+"F0.wireOp",EDGE,"E10"),sQuery(id+"F0.wireOp",EDGE,"E11"),sQuery(id+"F0.wireOp",EDGE,"E12"),sQuery(id+"F0.wireOp",EDGE,"E13"),sQuery(id+"F0.wireOp",EDGE,"E14"),sQuery(id+"F0.wireOp",EDGE,"E15.filletArc"),sQuery(id+"F0.wireOp",EDGE,"E16.filletArc"),sQuery(id+"F0.wireOp",EDGE,"E17.filletArc"),sQuery(id+"F0.wireOp",EDGE,"E18.filletArc"),sQuery(id+"F17.wireOp",EDGE,"E58")])]});
            transform(context, id + "F19", {"entities" : qUnion([Q0]), "transformType" : TransformType.TRANSLATION_3D, "dx" : -118 * mm, "dy" : 0 * mm, "dz" : 0 * mm, "makeCopy" : true});
        }
        {
            var Q0;
            Q0=makeQuery(id+"F18.opExtrude","CAP_FACE",FACE,{"disambiguationData":[OSD([sQuery(id+"F0.wireOp",EDGE,"E0"),sQuery(id+"F0.wireOp",EDGE,"E4"),sQuery(id+"F0.wireOp",EDGE,"E5"),sQuery(id+"F0.wireOp",EDGE,"E6"),sQuery(id+"F0.wireOp",EDGE,"E7"),sQuery(id+"F0.wireOp",EDGE,"E8"),sQuery(id+"F0.wireOp",EDGE,"E9"),sQuery(id+"F0.wireOp",EDGE,"E10"),sQuery(id+"F0.wireOp",EDGE,"E11"),sQuery(id+"F0.wireOp",EDGE,"E12"),sQuery(id+"F0.wireOp",EDGE,"E13"),sQuery(id+"F0.wireOp",EDGE,"E14"),sQuery(id+"F0.wireOp",EDGE,"E15.filletArc"),sQuery(id+"F0.wireOp",EDGE,"E16.filletArc"),sQuery(id+"F0.wireOp",EDGE,"E17.filletArc"),sQuery(id+"F0.wireOp",EDGE,"E18.filletArc"),sQuery(id+"F0.wireOp",EDGE,"E41.filletArc"),sQuery(id+"F0.wireOp",EDGE,"E42.filletArc"),sQuery(id+"F0.wireOp",EDGE,"E43.filletArc"),sQuery(id+"F17.wireOp",EDGE,"E58")])],"isStart":false});
            var sketch = newSketch(context, id + "F20", { "sketchPlane" : qUnion([Q0])});
            skLineSegment(sketch, "E59.0", {"start": v(213.55, 32.47) * mm, "end": v(207.44, 19.62) * mm});
            skLineSegment(sketch, "E59.1", {"start": v(269.4, 20.32) * mm, "end": v(263.67, 32.44) * mm});
            skArc(sketch, "E59.2", {"start": v(263.67, 32.44) * mm, "mid": v(258.87, 37.87) * mm, "end": v(251.92, 39.88) * mm});
            skLineSegment(sketch, "E59.3", {"start": v(251.92, 39.88) * mm, "end": v(225.3, 39.88) * mm});
            skArc(sketch, "E59.4", {"start": v(225.3, 39.88) * mm, "mid": v(218.35, 37.87) * mm, "end": v(213.55, 32.47) * mm});
            skLineSegment(sketch, "E60", {"start": v(207.44, 19.62) * mm, "end": v(205.34, 15.2) * mm});
            skLineSegment(sketch, "E61.0", {"start": v(37.27, 33.37) * mm, "end": v(31.28, 21.12) * mm});
            skLineSegment(sketch, "E61.1", {"start": v(94.8, 15.2) * mm, "end": v(85.19, 33.67) * mm});
            skArc(sketch, "E61.2", {"start": v(85.19, 33.67) * mm, "mid": v(80.4, 38.78) * mm, "end": v(73.66, 40.66) * mm});
            skLineSegment(sketch, "E61.3", {"start": v(73.66, 40.66) * mm, "end": v(48.95, 40.66) * mm});
            skArc(sketch, "E61.4", {"start": v(48.95, 40.66) * mm, "mid": v(42.06, 38.7) * mm, "end": v(37.27, 33.37) * mm});
            skLineSegment(sketch, "E62", {"start": v(31.28, 21.12) * mm, "end": v(29.12, 16.68) * mm});
            skSolve(sketch);
        }
        {
            var Q0;
            Q0=makeQuery(id+"F20.imprint","IMPRINT",FACE,{"disambiguationData":[TD([[makeQuery(id+"F20.imprint","IMPRINT",EDGE,{"derivedFrom":sQuery(id+"F20.wireOp",EDGE,"E61.0")}),1.0]])]});
            var Q1;
            Q1=makeQuery(id+"F20.imprint","IMPRINT",FACE,{"disambiguationData":[TD([[makeQuery(id+"F20.imprint","IMPRINT",EDGE,{"derivedFrom":sQuery(id+"F20.wireOp",EDGE,"E59.0")}),1.0]])]});
            extrude(context, id + "F21", {"entities" : qUnion([Q0, Q1]), "depth" : 8 * mm, "offsetDistance" : 25 * mm});
        }
        {
            var Q0;
            Q0=makeQuery(id+"F21.opExtrude","SWEPT_BODY",BODY,{"disambiguationData":[OSD([sQuery(id+"F0.wireOp",EDGE,"E6"),sQuery(id+"F0.wireOp",EDGE,"E7"),sQuery(id+"F0.wireOp",EDGE,"E8"),sQuery(id+"F0.wireOp",EDGE,"E9"),sQuery(id+"F0.wireOp",EDGE,"E10"),sQuery(id+"F0.wireOp",EDGE,"E17.filletArc"),sQuery(id+"F0.wireOp",EDGE,"E18.filletArc"),sQuery(id+"F0.wireOp",EDGE,"E41.filletArc"),sQuery(id+"F20.wireOp",EDGE,"E59.0"),sQuery(id+"F20.wireOp",EDGE,"E59.1"),sQuery(id+"F20.wireOp",EDGE,"E59.2"),sQuery(id+"F20.wireOp",EDGE,"E59.3"),sQuery(id+"F20.wireOp",EDGE,"E59.4"),sQuery(id+"F20.wireOp",EDGE,"E60")])]});
            transform(context, id + "F22", {"entities" : qUnion([Q0]), "transformType" : TransformType.TRANSLATION_3D, "dx" : -129 * mm, "dy" : 0 * mm, "dz" : 0 * mm, "makeCopy" : true});
        }
        {
            var Q0;
            Q0=makeQuery(id+"F21.opExtrude","SWEPT_BODY",BODY,{"disambiguationData":[OSD([sQuery(id+"F0.wireOp",EDGE,"E10"),sQuery(id+"F0.wireOp",EDGE,"E11"),sQuery(id+"F0.wireOp",EDGE,"E12"),sQuery(id+"F0.wireOp",EDGE,"E13"),sQuery(id+"F0.wireOp",EDGE,"E14"),sQuery(id+"F0.wireOp",EDGE,"E15.filletArc"),sQuery(id+"F0.wireOp",EDGE,"E16.filletArc"),sQuery(id+"F0.wireOp",EDGE,"E42.filletArc"),sQuery(id+"F0.wireOp",EDGE,"E43.filletArc"),sQuery(id+"F20.wireOp",EDGE,"E61.0"),sQuery(id+"F20.wireOp",EDGE,"E61.1"),sQuery(id+"F20.wireOp",EDGE,"E61.2"),sQuery(id+"F20.wireOp",EDGE,"E61.3"),sQuery(id+"F20.wireOp",EDGE,"E61.4"),sQuery(id+"F20.wireOp",EDGE,"E62")])]});
            transform(context, id + "F23", {"entities" : qUnion([Q0]), "transformType" : TransformType.TRANSLATION_3D, "dx" : -129 * mm, "dy" : 0 * mm, "dz" : 0 * mm, "makeCopy" : true});
        }
        {
            var Q0;
            Q0=makeQuery(id+"F6.opExtrude","SWEPT_FACE",FACE,{"disambiguationData":[OSD([sQuery(id+"F5.wireOp",EDGE,"E45.bottom")])]});
            var sketch = newSketch(context, id + "F24", { "sketchPlane" : qUnion([Q0])});
            skLineSegment(sketch, "E63", {"start": v(88.73, 270.97) * mm, "end": v(112, 196.81) * mm});
            skLineSegment(sketch, "E64", {"start": v(112, 196.81) * mm, "end": v(3, 196.81) * mm});
            skLineSegment(sketch, "E65", {"start": v(3, 196.81) * mm, "end": v(26.27, 270.97) * mm});
            skPoint(sketch, "E66", {"position": v(57.5, 270.97) * mm});
            skLineSegment(sketch, "E67", {"start": v(57.5, 270.97) * mm, "end": v(57.5, 270.97) * mm});
            skLineSegment(sketch, "E68", {"start": v(26.27, 270.97) * mm, "end": v(57.5, 270.97) * mm});
            skLineSegment(sketch, "E69", {"start": v(88.73, 270.97) * mm, "end": v(57.5, 270.97) * mm});
            skSolve(sketch);
        }
        {
            var Q0;
            Q0 = qSketchRegion(id + "F24", true);
            extrude(context, id + "F25", {"entities" : qUnion([Q0]), "depth" : 8 * mm, "offsetDistance" : 25 * mm});
        }
        {
            var Q0;
            Q0=makeQuery(id+"F14.opExtrude","SWEPT_FACE",FACE,{"disambiguationData":[OSD([sQuery(id+"F13.wireOp",EDGE,"E56.bottom")])]});
            var sketch = newSketch(context, id + "F26", { "sketchPlane" : qUnion([Q0])});
            skLineSegment(sketch, "E70.bottom", {"start": v(0, 6.05) * mm, "end": v(115, 6.05) * mm});
            skLineSegment(sketch, "E70.top", {"start": v(0, 180.01) * mm, "end": v(115, 180.01) * mm});
            skLineSegment(sketch, "E70.left", {"start": v(0, 6.05) * mm, "end": v(0, 180.01) * mm});
            skLineSegment(sketch, "E70.right", {"start": v(115, 6.05) * mm, "end": v(115, 180.01) * mm});
            skSolve(sketch);
        }
        {
            var Q0;
            Q0 = qSketchRegion(id + "F26", true);
            extrude(context, id + "F27", {"entities" : qUnion([Q0]), "depth" : 8 * mm, "offsetDistance" : 25 * mm});
        }
        {
            var Q0;
            Q0=makeQuery(id+"F27.opExtrude","SWEPT_FACE",FACE,{"disambiguationData":[OSD([sQuery(id+"F26.wireOp",EDGE,"E70.right")])]});
            var sketch = newSketch(context, id + "F28", { "sketchPlane" : qUnion([Q0])});
            skLineSegment(sketch, "E71", {"start": v(180.01, 93.72) * mm, "end": v(178.29, 94.64) * mm});
            skLineSegment(sketch, "E72", {"start": v(176.64, 95.18) * mm, "end": v(131.25, 101.72) * mm});
            skPoint(sketch, "E73.visualSharp", {"position": v(177.51, 95.06) * mm});
            skArc(sketch, "E73.filletArc", {"start": v(178.29, 94.64) * mm, "mid": v(177.49, 94.98) * mm, "end": v(176.64, 95.18) * mm});
            skSolve(sketch);
        }
        {
            var Q0;
            Q0 = qSketchRegion(id + "F28", true);
            var Q1;
            Q1=makeQuery(id+"F28.imprint","IMPRINT",FACE,{"disambiguationData":[TD([[makeQuery(id+"F28.imprint","IMPRINT",EDGE,{"derivedFrom":sQuery(id+"F28.wireOp",EDGE,"E71")}),-1.0]])]});
            extrude(context, id + "F29", {"entities" : qUnion([Q0, Q1]), "operationType" : NewBodyOperationType.REMOVE, "oppositeDirection" : true, "depth" : 126.6 * mm, "offsetDistance" : 25 * mm});
        }
        {
            var Q0;
            Q0=makeQuery(id+"F27.opExtrude","CAP_EDGE",EDGE,{"disambiguationData":[OSD([sQuery(id+"F26.wireOp",EDGE,"E70.right")])],"isStart":false});
            var Q1;
            Q1=makeQuery(id+"F29.boolean.opBoolean","COPY",EDGE,{"derivedFrom":makeQuery(id+"F29.opExtrude","CAP_EDGE",EDGE,{"disambiguationData":[OSD([sQuery(id+"F28.wireOp",EDGE,"E72")])],"isStart":true})});
            var Q2;
            Q2=makeQuery(id+"F29.boolean.opBoolean","INTERSECT",EDGE,{"derivedFrom":[makeQuery(id+"F27.opExtrude","SWEPT_FACE",FACE,{"disambiguationData":[OSD([sQuery(id+"F26.wireOp",EDGE,"E70.left")])]}),makeQuery(id+"F29.opExtrude","SWEPT_FACE",FACE,{"disambiguationData":[OSD([sQuery(id+"F28.wireOp",EDGE,"E72")])]})]});
            var Q3;
            Q3=makeQuery(id+"F29.boolean.opBoolean","INTERSECT",EDGE,{"derivedFrom":[makeQuery(id+"F27.opExtrude","SWEPT_FACE",FACE,{"disambiguationData":[OSD([sQuery(id+"F26.wireOp",EDGE,"E70.left")])]}),makeQuery(id+"F29.opExtrude","SWEPT_FACE",FACE,{"disambiguationData":[OSD([sQuery(id+"F28.wireOp",EDGE,"E73.filletArc")])]})]});
            var Q4;
            Q4=makeQuery(id+"F29.boolean.opBoolean","INTERSECT",EDGE,{"derivedFrom":[makeQuery(id+"F27.opExtrude","SWEPT_FACE",FACE,{"disambiguationData":[OSD([sQuery(id+"F26.wireOp",EDGE,"E70.left")])]}),makeQuery(id+"F29.opExtrude","SWEPT_FACE",FACE,{"disambiguationData":[OSD([sQuery(id+"F28.wireOp",EDGE,"E71")])]})]});
            var Q5;
            Q5=makeQuery(id+"F29.boolean.opBoolean","COPY",EDGE,{"derivedFrom":makeQuery(id+"F29.opExtrude","CAP_EDGE",EDGE,{"disambiguationData":[OSD([sQuery(id+"F28.wireOp",EDGE,"E73.filletArc")])],"isStart":true})});
            var Q6;
            Q6=makeQuery(id+"F29.boolean.opBoolean","COPY",EDGE,{"derivedFrom":makeQuery(id+"F29.opExtrude","CAP_EDGE",EDGE,{"disambiguationData":[OSD([sQuery(id+"F28.wireOp",EDGE,"E71")])],"isStart":true})});
            var Q7;
            Q7=makeQuery(id+"F27.opExtrude","CAP_EDGE",EDGE,{"disambiguationData":[OSD([sQuery(id+"F26.wireOp",EDGE,"E70.left")])],"isStart":false});
            fillet(context, id + "F30", {"entities" : qUnion([Q0, Q1, Q2, Q3, Q4, Q5, Q6, Q7]), "radius" : 7 * mm, "tangentPropagation" : true, "allowEdgeOverflow" : false});
        }
        {
            var Q0;
            Q0=makeQuery(id+"F25.opExtrude","CAP_EDGE",EDGE,{"disambiguationData":[OSD([sQuery(id+"F24.wireOp",EDGE,"E63")])],"isStart":false});
            var Q1;
            Q1=makeQuery(id+"F25.opExtrude","CAP_EDGE",EDGE,{"disambiguationData":[OSD([sQuery(id+"F24.wireOp",EDGE,"E68"),sQuery(id+"F24.wireOp",EDGE,"E69")])],"isStart":false});
            var Q2;
            Q2=makeQuery(id+"F25.opExtrude","CAP_EDGE",EDGE,{"disambiguationData":[OSD([sQuery(id+"F24.wireOp",EDGE,"E65")])],"isStart":false});
            fillet(context, id + "F31", {"entities" : qUnion([Q0, Q1, Q2]), "radius" : 7 * mm, "tangentPropagation" : true, "allowEdgeOverflow" : false});
        }
        {
            var Q0;
            Q0=makeQuery(id+"F21.opExtrude","CAP_EDGE",EDGE,{"disambiguationData":[OSD([sQuery(id+"F20.wireOp",EDGE,"E61.0"),sQuery(id+"F20.wireOp",EDGE,"E62")])],"isStart":false});
            var Q1;
            Q1=makeQuery(id+"F21.opExtrude","CAP_EDGE",EDGE,{"disambiguationData":[OSD([sQuery(id+"F20.wireOp",EDGE,"E61.4")])],"isStart":false});
            var Q2;
            Q2=makeQuery(id+"F21.opExtrude","CAP_EDGE",EDGE,{"disambiguationData":[OSD([sQuery(id+"F20.wireOp",EDGE,"E59.3")])],"isStart":false});
            var Q3;
            Q3=makeQuery(id+"F22.opPattern","COPY",EDGE,{"derivedFrom":makeQuery(id+"F21.opExtrude","CAP_EDGE",EDGE,{"disambiguationData":[OSD([sQuery(id+"F20.wireOp",EDGE,"E59.3")])],"isStart":true}),"instanceName":"1"});
            var Q4;
            Q4=makeQuery(id+"F23.opPattern","COPY",EDGE,{"derivedFrom":makeQuery(id+"F21.opExtrude","CAP_EDGE",EDGE,{"disambiguationData":[OSD([sQuery(id+"F20.wireOp",EDGE,"E61.3")])],"isStart":true}),"instanceName":"1"});
            fillet(context, id + "F32", {"entities" : qUnion([Q0, Q1, Q2, Q3, Q4]), "radius" : 7 * mm, "tangentPropagation" : true, "allowEdgeOverflow" : false});
        }
        {
            var Q0;
            Q0=makeQuery(id+"F18.opExtrude","CAP_EDGE",EDGE,{"disambiguationData":[OSD([sQuery(id+"F0.wireOp",EDGE,"E4"),sQuery(id+"F17.wireOp",EDGE,"E58")])],"isStart":false});
            var Q1;
            Q1=makeQuery(id+"F19.opPattern","COPY",EDGE,{"derivedFrom":makeQuery(id+"F18.opExtrude","CAP_EDGE",EDGE,{"disambiguationData":[OSD([sQuery(id+"F0.wireOp",EDGE,"E4"),sQuery(id+"F17.wireOp",EDGE,"E58")])],"isStart":true}),"instanceName":"1"});
            var Q2;
            Q2=makeQuery(id+"F18.opExtrude","CAP_EDGE",EDGE,{"disambiguationData":[OSD([sQuery(id+"F0.wireOp",EDGE,"E5")])],"isStart":false});
            var Q3;
            Q3=makeQuery(id+"F19.opPattern","COPY",EDGE,{"derivedFrom":makeQuery(id+"F18.opExtrude","CAP_EDGE",EDGE,{"disambiguationData":[OSD([sQuery(id+"F0.wireOp",EDGE,"E5")])],"isStart":true}),"instanceName":"1"});
            fillet(context, id + "F33", {"entities" : qUnion([Q0, Q1, Q2, Q3]), "radius" : 5 * mm, "tangentPropagation" : true, "allowEdgeOverflow" : false});
        }
        {
            var Q0;
            Q0=makeQuery(id+"F16.opExtrude","SWEPT_FACE",FACE,{"disambiguationData":[OSD([sQuery(id+"F15.wireOp",EDGE,"E57.left")])]});
            var sketch = newSketch(context, id + "F34", { "sketchPlane" : qUnion([Q0])});
            skLineSegment(sketch, "E74.bottom", {"start": v(38.55, 85.72) * mm, "end": v(76.45, 85.72) * mm});
            skLineSegment(sketch, "E74.top", {"start": v(38.55, 58.07) * mm, "end": v(76.45, 58.07) * mm});
            skLineSegment(sketch, "E74.left", {"start": v(34.55, 81.72) * mm, "end": v(34.55, 62.07) * mm});
            skLineSegment(sketch, "E74.right", {"start": v(80.45, 81.72) * mm, "end": v(80.45, 62.07) * mm});
            skLineSegment(sketch, "E75", {"start": v(57.5, 90.72) * mm, "end": v(57.5, 85.72) * mm});
            skPoint(sketch, "E76.visualSharp", {"position": v(34.55, 85.72) * mm});
            skArc(sketch, "E76.filletArc", {"start": v(38.55, 85.72) * mm, "mid": v(35.72, 84.55) * mm, "end": v(34.55, 81.72) * mm});
            skPoint(sketch, "E77.visualSharp", {"position": v(80.45, 85.72) * mm});
            skArc(sketch, "E77.filletArc", {"start": v(80.45, 81.72) * mm, "mid": v(79.28, 84.55) * mm, "end": v(76.45, 85.72) * mm});
            skPoint(sketch, "E78.visualSharp", {"position": v(80.45, 58.07) * mm});
            skArc(sketch, "E78.filletArc", {"start": v(76.45, 58.07) * mm, "mid": v(79.28, 59.24) * mm, "end": v(80.45, 62.07) * mm});
            skPoint(sketch, "E79.visualSharp", {"position": v(34.55, 58.07) * mm});
            skArc(sketch, "E79.filletArc", {"start": v(34.55, 62.07) * mm, "mid": v(35.72, 59.24) * mm, "end": v(38.55, 58.07) * mm});
            skLineSegment(sketch, "E80.bottom", {"start": v(97.8, 83.92) * mm, "end": v(101.07, 83.92) * mm});
            skLineSegment(sketch, "E80.top", {"start": v(97.8, 58.07) * mm, "end": v(101.07, 58.07) * mm});
            skLineSegment(sketch, "E80.left", {"start": v(93.8, 79.92) * mm, "end": v(93.8, 62.07) * mm});
            skLineSegment(sketch, "E80.right", {"start": v(105.07, 79.92) * mm, "end": v(105.07, 62.07) * mm});
            skPoint(sketch, "E81.visualSharp", {"position": v(93.8, 83.92) * mm});
            skArc(sketch, "E81.filletArc", {"start": v(97.8, 83.92) * mm, "mid": v(94.98, 82.75) * mm, "end": v(93.8, 79.92) * mm});
            skPoint(sketch, "E82.visualSharp", {"position": v(105.07, 83.92) * mm});
            skArc(sketch, "E82.filletArc", {"start": v(105.07, 79.92) * mm, "mid": v(103.9, 82.75) * mm, "end": v(101.07, 83.92) * mm});
            skPoint(sketch, "E83.visualSharp", {"position": v(105.07, 58.07) * mm});
            skArc(sketch, "E83.filletArc", {"start": v(101.07, 58.07) * mm, "mid": v(103.9, 59.24) * mm, "end": v(105.07, 62.07) * mm});
            skPoint(sketch, "E84.visualSharp", {"position": v(93.8, 58.07) * mm});
            skArc(sketch, "E84.filletArc", {"start": v(93.8, 62.07) * mm, "mid": v(94.98, 59.24) * mm, "end": v(97.8, 58.07) * mm});
            skArc(sketch, "E85.MirrorCS", {"start": v(17.2, 83.92) * mm, "mid": v(20.02, 82.75) * mm, "end": v(21.2, 79.92) * mm});
            skLineSegment(sketch, "E86.MirrorCS", {"start": v(17.2, 83.92) * mm, "end": v(13.93, 83.92) * mm});
            skArc(sketch, "E87.MirrorCS", {"start": v(9.93, 79.92) * mm, "mid": v(11.1, 82.75) * mm, "end": v(13.93, 83.92) * mm});
            skLineSegment(sketch, "E88.MirrorCS", {"start": v(9.93, 79.92) * mm, "end": v(9.93, 62.07) * mm});
            skArc(sketch, "E89.MirrorCS", {"start": v(13.93, 58.07) * mm, "mid": v(11.1, 59.24) * mm, "end": v(9.93, 62.07) * mm});
            skLineSegment(sketch, "E90.MirrorCS", {"start": v(17.2, 58.07) * mm, "end": v(13.93, 58.07) * mm});
            skArc(sketch, "E91.MirrorCS", {"start": v(21.2, 62.07) * mm, "mid": v(20.02, 59.24) * mm, "end": v(17.2, 58.07) * mm});
            skLineSegment(sketch, "E92.MirrorCS", {"start": v(21.2, 79.92) * mm, "end": v(21.2, 62.07) * mm});
            skSolve(sketch);
        }
        {
            var Q0;
            Q0=makeQuery(id+"F34.imprint","IMPRINT",FACE,{"disambiguationData":[TD([[makeQuery(id+"F34.imprint","IMPRINT",EDGE,{"derivedFrom":sQuery(id+"F34.wireOp",EDGE,"E74.top")}),1.0]])]});
            var Q1;
            Q1=makeQuery(id+"F34.imprint","IMPRINT",FACE,{"disambiguationData":[TD([[makeQuery(id+"F34.imprint","IMPRINT",EDGE,{"derivedFrom":sQuery(id+"F34.wireOp",EDGE,"E85.MirrorCS")}),-1.0]])]});
            var Q2;
            Q2=makeQuery(id+"F34.imprint","IMPRINT",FACE,{"disambiguationData":[TD([[makeQuery(id+"F34.imprint","IMPRINT",EDGE,{"derivedFrom":sQuery(id+"F34.wireOp",EDGE,"E80.bottom")}),-1.0]])]});
            extrude(context, id + "F35", {"entities" : qUnion([Q0, Q1, Q2]), "operationType" : NewBodyOperationType.REMOVE, "oppositeDirection" : true, "depth" : 25 * mm, "offsetDistance" : 25 * mm});
        }
        {
            var Q0;
            Q0=makeQuery(id+"F4.opExtrude","SWEPT_FACE",FACE,{"disambiguationData":[OSD([sQuery(id+"F3.wireOp",EDGE,"E44.top")])]});
            var sketch = newSketch(context, id + "F36", { "sketchPlane" : qUnion([Q0])});
            skLineSegment(sketch, "E93.bottom", {"start": v(-11, -263.87) * mm, "end": v(126, -263.87) * mm});
            skLineSegment(sketch, "E93.top", {"start": v(-11, -274.7) * mm, "end": v(126, -274.7) * mm});
            skLineSegment(sketch, "E93.left", {"start": v(-11, -263.87) * mm, "end": v(-11, -274.7) * mm});
            skLineSegment(sketch, "E93.right", {"start": v(126, -263.87) * mm, "end": v(126, -274.7) * mm});
            skLineSegment(sketch, "E94.bottom", {"start": v(126, -263.87) * mm, "end": v(-11, -263.87) * mm});
            skLineSegment(sketch, "E94.top", {"start": v(126, -274.7) * mm, "end": v(-11, -274.7) * mm});
            skSolve(sketch);
        }
        {
            var Q0;
            Q0 = qSketchRegion(id + "F36", true);
            extrude(context, id + "F37", {"entities" : qUnion([Q0]), "depth" : 8 * mm, "offsetDistance" : 25 * mm});
        }
        {
            var Q0;
            Q0=makeQuery(id+"F37.opExtrude","SWEPT_BODY",BODY,{"disambiguationData":[OSD([sQuery(id+"F36.wireOp",EDGE,"E94.bottom"),sQuery(id+"F36.wireOp",EDGE,"E94.top"),sQuery(id+"F36.wireOp",EDGE,"E93.right"),sQuery(id+"F36.wireOp",EDGE,"E93.left")])]});
            transform(context, id + "F38", {"entities" : qUnion([Q0]), "transformType" : TransformType.TRANSLATION_3D, "dx" : 0 * mm, "dy" : 3.8 * mm, "dz" : 0 * mm, "makeCopy" : false});
        }
        {
            var Q0;
            Q0=makeQuery(id+"F37.opExtrude","SWEPT_EDGE",EDGE,{"disambiguationData":[OSD([sQuery(id+"F36.wireOp",EDGE,"E94.top"),sQuery(id+"F36.wireOp",EDGE,"E93.left")])]});
            var Q1;
            Q1=makeQuery(id+"F37.opExtrude","SWEPT_EDGE",EDGE,{"disambiguationData":[OSD([sQuery(id+"F36.wireOp",EDGE,"E94.top"),sQuery(id+"F36.wireOp",EDGE,"E93.right")])]});
            fillet(context, id + "F39", {"entities" : qUnion([Q0, Q1]), "radius" : 7 * mm, "tangentPropagation" : true, "allowEdgeOverflow" : false});
        }
        {
            var Q0;
            Q0=makeQuery(id+"F4.opExtrude","SWEPT_FACE",FACE,{"disambiguationData":[OSD([sQuery(id+"F3.wireOp",EDGE,"E44.left")])]});
            var sketch = newSketch(context, id + "F40", { "sketchPlane" : qUnion([Q0])});
            skLineSegment(sketch, "E95", {"start": v(-57.5, 52.3) * mm, "end": v(-57.5, 20.32) * mm});
            skLineSegment(sketch, "E96.bottom", {"start": v(-106, 49.05) * mm, "end": v(-92, 49.05) * mm});
            skLineSegment(sketch, "E96.top", {"start": v(-106, 29.05) * mm, "end": v(-92, 29.05) * mm});
            skLineSegment(sketch, "E96.left", {"start": v(-109, 46.05) * mm, "end": v(-109, 32.05) * mm});
            skLineSegment(sketch, "E96.right", {"start": v(-89, 46.05) * mm, "end": v(-89, 32.05) * mm});
            skPoint(sketch, "E97.visualSharp", {"position": v(-109, 49.05) * mm});
            skArc(sketch, "E97.filletArc", {"start": v(-106, 49.05) * mm, "mid": v(-108.12, 48.17) * mm, "end": v(-109, 46.05) * mm});
            skPoint(sketch, "E98.visualSharp", {"position": v(-89, 49.05) * mm});
            skArc(sketch, "E98.filletArc", {"start": v(-89, 46.05) * mm, "mid": v(-89.88, 48.17) * mm, "end": v(-92, 49.05) * mm});
            skPoint(sketch, "E99.visualSharp", {"position": v(-89, 29.05) * mm});
            skArc(sketch, "E99.filletArc", {"start": v(-92, 29.05) * mm, "mid": v(-89.88, 29.93) * mm, "end": v(-89, 32.05) * mm});
            skPoint(sketch, "E100.visualSharp", {"position": v(-109, 29.05) * mm});
            skArc(sketch, "E100.filletArc", {"start": v(-109, 32.05) * mm, "mid": v(-108.12, 29.93) * mm, "end": v(-106, 29.05) * mm});
            skLineSegment(sketch, "E101.0", {"start": v(-106, 48.05) * mm, "end": v(-92, 48.05) * mm});
            skArc(sketch, "E101.1", {"start": v(-90, 46.05) * mm, "mid": v(-90.58, 47.46) * mm, "end": v(-92, 48.05) * mm});
            skArc(sketch, "E101.2", {"start": v(-106, 48.05) * mm, "mid": v(-107.41, 47.46) * mm, "end": v(-108, 46.05) * mm});
            skLineSegment(sketch, "E101.3", {"start": v(-90, 46.05) * mm, "end": v(-90, 32.05) * mm});
            skLineSegment(sketch, "E101.4", {"start": v(-108, 46.05) * mm, "end": v(-108, 32.05) * mm});
            skArc(sketch, "E101.5", {"start": v(-108, 32.05) * mm, "mid": v(-107.41, 30.63) * mm, "end": v(-106, 30.05) * mm});
            skLineSegment(sketch, "E101.6", {"start": v(-106, 30.05) * mm, "end": v(-92, 30.05) * mm});
            skArc(sketch, "E101.7", {"start": v(-92, 30.05) * mm, "mid": v(-90.58, 30.63) * mm, "end": v(-90, 32.05) * mm});
            skCircle(sketch, "E102", {"center": v(-97.38, 40) * mm, "radius": 5.64 * mm});
            skCircle(sketch, "E103", {"center": v(-105.4, 45.53) * mm, "radius": 1.75 * mm});
            skCircle(sketch, "E104", {"center": v(-105.4, 35.08) * mm, "radius": 1.75 * mm});
            skArc(sketch, "E105.MirrorCS", {"start": v(-9, 48.05) * mm, "mid": v(-7.59, 47.46) * mm, "end": v(-7, 46.05) * mm});
            skArc(sketch, "E106.MirrorCS", {"start": v(-9, 49.05) * mm, "mid": v(-6.88, 48.17) * mm, "end": v(-6, 46.05) * mm});
            skArc(sketch, "E107.MirrorCS", {"start": v(-23, 30.05) * mm, "mid": v(-24.42, 30.63) * mm, "end": v(-25, 32.05) * mm});
            skLineSegment(sketch, "E108.MirrorCS", {"start": v(-9, 49.05) * mm, "end": v(-23, 49.05) * mm});
            skArc(sketch, "E109.MirrorCS", {"start": v(-6, 32.05) * mm, "mid": v(-6.88, 29.93) * mm, "end": v(-9, 29.05) * mm});
            skCircle(sketch, "E110.MirrorC", {"center": v(-17.62, 40) * mm, "radius": 5.64 * mm});
            skArc(sketch, "E111.MirrorCS", {"start": v(-7, 32.05) * mm, "mid": v(-7.59, 30.63) * mm, "end": v(-9, 30.05) * mm});
            skArc(sketch, "E112.MirrorCS", {"start": v(-23, 29.05) * mm, "mid": v(-25.12, 29.93) * mm, "end": v(-26, 32.05) * mm});
            skArc(sketch, "E113.MirrorCS", {"start": v(-25, 46.05) * mm, "mid": v(-24.42, 47.46) * mm, "end": v(-23, 48.05) * mm});
            skArc(sketch, "E114.MirrorCS", {"start": v(-26, 46.05) * mm, "mid": v(-25.12, 48.17) * mm, "end": v(-23, 49.05) * mm});
            skLineSegment(sketch, "E115.MirrorCS", {"start": v(-9, 29.05) * mm, "end": v(-23, 29.05) * mm});
            skLineSegment(sketch, "E116.MirrorCS", {"start": v(-26, 46.05) * mm, "end": v(-26, 32.05) * mm});
            skPoint(sketch, "E117.MirrorP", {"position": v(-26, 49.05) * mm});
            skCircle(sketch, "E118.MirrorC", {"center": v(-9.6, 45.53) * mm, "radius": 1.75 * mm});
            skCircle(sketch, "E119.MirrorC", {"center": v(-9.6, 35.08) * mm, "radius": 1.75 * mm});
            skPoint(sketch, "E120.MirrorP", {"position": v(-6, 49.05) * mm});
            skPoint(sketch, "E121.MirrorP", {"position": v(-6, 29.05) * mm});
            skLineSegment(sketch, "E122.MirrorCS", {"start": v(-6, 46.05) * mm, "end": v(-6, 32.05) * mm});
            skLineSegment(sketch, "E123.MirrorCS", {"start": v(-9, 48.05) * mm, "end": v(-23, 48.05) * mm});
            skPoint(sketch, "E124.MirrorP", {"position": v(-26, 29.05) * mm});
            skLineSegment(sketch, "E125.MirrorCS", {"start": v(-9, 30.05) * mm, "end": v(-23, 30.05) * mm});
            skLineSegment(sketch, "E126.MirrorCS", {"start": v(-7, 46.05) * mm, "end": v(-7, 32.05) * mm});
            skLineSegment(sketch, "E127.MirrorCS", {"start": v(-25, 46.05) * mm, "end": v(-25, 32.05) * mm});
            skSolve(sketch);
        }
        {
            var Q0;
            Q0=makeQuery(id+"F40.imprint","IMPRINT",FACE,{"disambiguationData":[TD([[makeQuery(id+"F40.imprint","IMPRINT",EDGE,{"derivedFrom":sQuery(id+"F40.wireOp",EDGE,"E96.bottom")}),-1.0]])]});
            var Q1;
            Q1=makeQuery(id+"F40.imprint","IMPRINT",FACE,{"disambiguationData":[TD([[makeQuery(id+"F40.imprint","IMPRINT",EDGE,{"derivedFrom":sQuery(id+"F40.wireOp",EDGE,"yOWV3db2-J0nh-HN7o-hahv-vkZdsQXniM1Q")}),1.0]])]});
            var Q2;
            Q2=makeQuery(id+"F40.imprint","IMPRINT",FACE,{"disambiguationData":[TD([[makeQuery(id+"F40.imprint","IMPRINT",EDGE,{"derivedFrom":sQuery(id+"F40.wireOp",EDGE,"E103")}),1.0]])]});
            var Q3;
            Q3=makeQuery(id+"F40.imprint","IMPRINT",FACE,{"disambiguationData":[TD([[makeQuery(id+"F40.imprint","IMPRINT",EDGE,{"derivedFrom":sQuery(id+"F40.wireOp",EDGE,"E102")}),1.0]])]});
            var Q4;
            Q4=makeQuery(id+"F40.imprint","IMPRINT",FACE,{"disambiguationData":[TD([[makeQuery(id+"F40.imprint","IMPRINT",EDGE,{"derivedFrom":sQuery(id+"F40.wireOp",EDGE,"72eabaff-906d-4123-a2dc-fb9848d343120.MirrorCS")}),1.0]])]});
            var Q5;
            Q5=makeQuery(id+"F40.imprint","IMPRINT",FACE,{"disambiguationData":[TD([[makeQuery(id+"F40.imprint","IMPRINT",EDGE,{"derivedFrom":sQuery(id+"F40.wireOp",EDGE,"72eabaff-906d-4123-a2dc-fb9848d3431218.MirrorC")}),-1.0]])]});
            var Q6;
            Q6=makeQuery(id+"F40.imprint","IMPRINT",FACE,{"disambiguationData":[TD([[makeQuery(id+"F40.imprint","IMPRINT",EDGE,{"derivedFrom":sQuery(id+"F40.wireOp",EDGE,"72eabaff-906d-4123-a2dc-fb9848d3431219.MirrorC")}),-1.0]])]});
            var Q7;
            Q7=makeQuery(id+"F40.imprint","IMPRINT",FACE,{"disambiguationData":[TD([[makeQuery(id+"F40.imprint","IMPRINT",EDGE,{"derivedFrom":sQuery(id+"F40.wireOp",EDGE,"72eabaff-906d-4123-a2dc-fb9848d3431212.MirrorC")}),-1.0]])]});
            var Q8;
            Q8=makeQuery(id+"F40.imprint","IMPRINT",FACE,{"disambiguationData":[TD([[makeQuery(id+"F40.imprint","IMPRINT",EDGE,{"derivedFrom":sQuery(id+"F40.wireOp",EDGE,"E105.MirrorCS")}),1.0]])]});
            var Q9;
            Q9=makeQuery(id+"F40.imprint","IMPRINT",FACE,{"disambiguationData":[TD([[makeQuery(id+"F40.imprint","IMPRINT",EDGE,{"derivedFrom":sQuery(id+"F40.wireOp",EDGE,"E110.MirrorC")}),-1.0]])]});
            var Q10;
            Q10=makeQuery(id+"F40.imprint","IMPRINT",FACE,{"disambiguationData":[TD([[makeQuery(id+"F40.imprint","IMPRINT",EDGE,{"derivedFrom":sQuery(id+"F40.wireOp",EDGE,"E119.MirrorC")}),-1.0]])]});
            var Q11;
            Q11=makeQuery(id+"F40.imprint","IMPRINT",FACE,{"disambiguationData":[TD([[makeQuery(id+"F40.imprint","IMPRINT",EDGE,{"derivedFrom":sQuery(id+"F40.wireOp",EDGE,"E118.MirrorC")}),-1.0]])]});
            var Q12;
            Q12=makeQuery(id+"F40.imprint","IMPRINT",FACE,{"disambiguationData":[TD([[makeQuery(id+"F40.imprint","IMPRINT",EDGE,{"derivedFrom":sQuery(id+"F40.wireOp",EDGE,"E104")}),1.0]])]});
            extrude(context, id + "F41", {"entities" : qUnion([Q0, Q1, Q2, Q3, Q4, Q5, Q6, Q7, Q8, Q9, Q10, Q11, Q12]), "depth" : 1 * mm, "offsetDistance" : 25 * mm});
        }
        {
            var Q0;
            Q0=makeQuery(id+"F4.opExtrude","SWEPT_FACE",FACE,{"disambiguationData":[OSD([sQuery(id+"F3.wireOp",EDGE,"E44.left")])]});
            var sketch = newSketch(context, id + "F42", { "sketchPlane" : qUnion([Q0])});
            skLineSegment(sketch, "E128.bottom", {"start": v(-88.73, 52.3) * mm, "end": v(-26.27, 52.3) * mm});
            skLineSegment(sketch, "E128.top", {"start": v(-88.73, 24.51) * mm, "end": v(-26.27, 24.51) * mm});
            skLineSegment(sketch, "E128.left", {"start": v(-88.73, 52.3) * mm, "end": v(-88.73, 24.51) * mm});
            skLineSegment(sketch, "E128.right", {"start": v(-26.27, 52.3) * mm, "end": v(-26.27, 24.51) * mm});
            skSolve(sketch);
        }
        {
            var Q0;
            Q0=makeQuery(id+"F42.imprint","IMPRINT",FACE,{"disambiguationData":[TD([[makeQuery(id+"F42.imprint","IMPRINT",EDGE,{"derivedFrom":sQuery(id+"F42.wireOp",EDGE,"E128.bottom")}),-1.0]])]});
            extrude(context, id + "F43", {"entities" : qUnion([Q0]), "depth" : 3 * mm, "offsetDistance" : 25 * mm});
        }
    });
